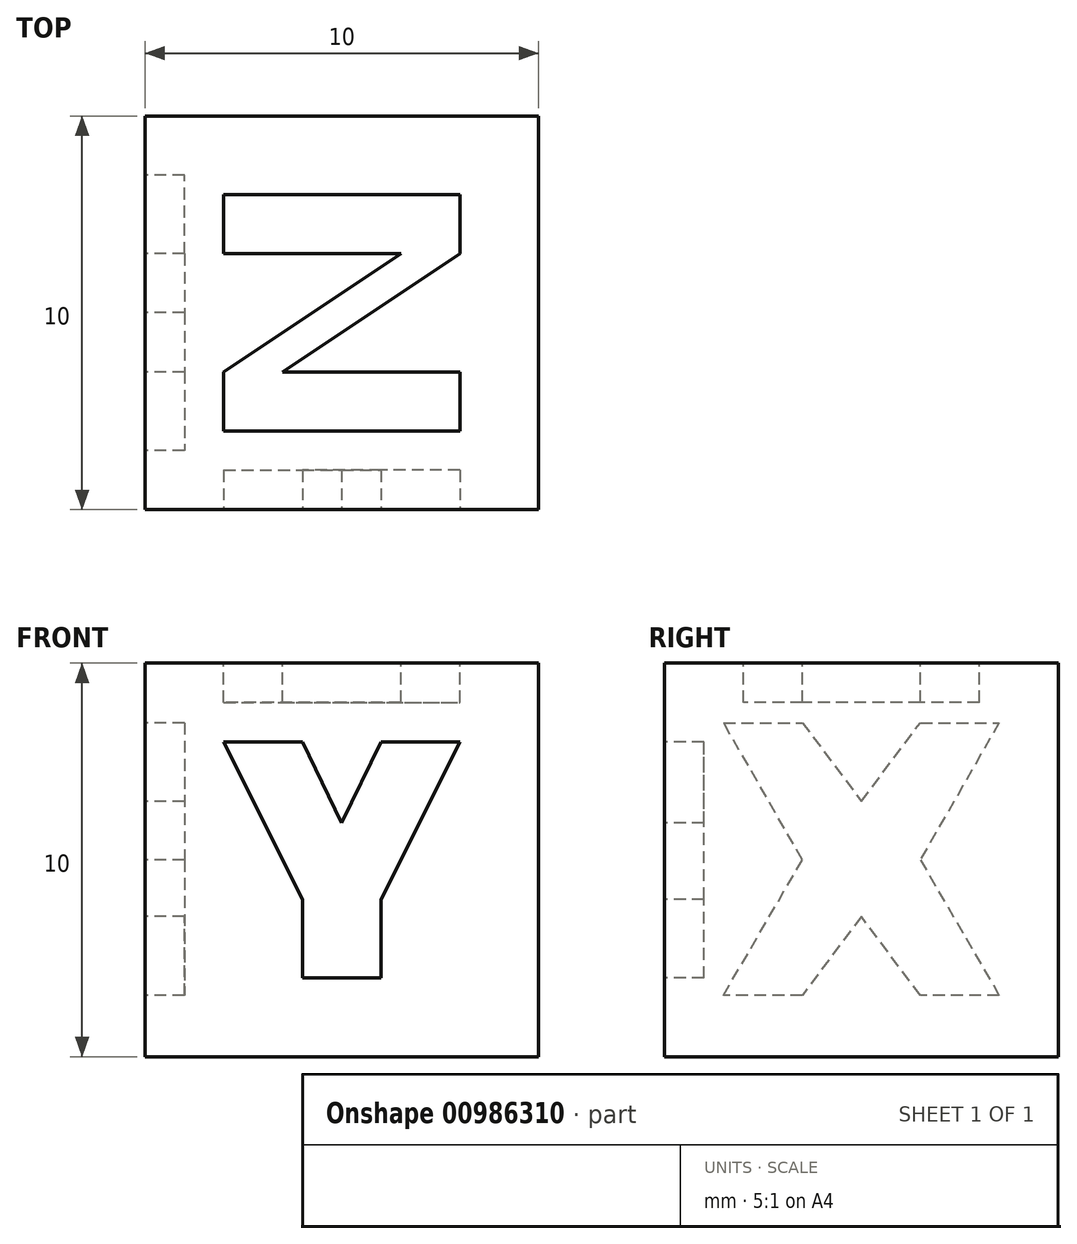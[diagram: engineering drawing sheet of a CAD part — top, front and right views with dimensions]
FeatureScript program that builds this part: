
annotation { "Feature Type Name" : "Feature", "Feature Type Description" : "" }
export const myFeature = defineFeature(function(context is Context, id is Id, definition is map)
    precondition{}
    {
        {
            var Q0;
            Q0=qCreatedBy(makeId("Top.planeOp"),FACE);
            var sketch = newSketch(context, id + "F0", { "sketchPlane" : qUnion([Q0])});
            skLineSegment(sketch, "E0.bottom", {"start": v(0, 0) * mm, "end": v(10, 0) * mm});
            skLineSegment(sketch, "E0.top", {"start": v(0, 10) * mm, "end": v(10, 10) * mm});
            skLineSegment(sketch, "E0.left", {"start": v(0, 0) * mm, "end": v(0, 10) * mm});
            skLineSegment(sketch, "E0.right", {"start": v(10, 0) * mm, "end": v(10, 10) * mm});
            skSolve(sketch);
        }
        {
            var Q0;
            Q0=makeQuery(id+"F0.imprint","IMPRINT",FACE,{"disambiguationData":[TD([[makeQuery(id+"F0.imprint","IMPRINT",EDGE,{"derivedFrom":sQuery(id+"F0.wireOp",EDGE,"E0.bottom")}),1.0]])]});
            extrude(context, id + "F1", {"entities" : qUnion([Q0]), "depth" : 10 * mm, "offsetDistance" : 25 * mm});
        }
        {
            var Q0;
            Q0=makeQuery(id+"F1.opExtrude","SWEPT_FACE",FACE,{"disambiguationData":[OSD([sQuery(id+"F0.wireOp",EDGE,"E0.bottom")])]});
            var sketch = newSketch(context, id + "F2", { "sketchPlane" : qUnion([Q0])});
            skLineSegment(sketch, "E1", {"start": v(2, 8) * mm, "end": v(4, 8) * mm});
            skLineSegment(sketch, "E2", {"start": v(4, 8) * mm, "end": v(5, 5.94) * mm});
            skLineSegment(sketch, "E3", {"start": v(5, 5.94) * mm, "end": v(6, 8) * mm});
            skLineSegment(sketch, "E4", {"start": v(6, 8) * mm, "end": v(8, 8) * mm});
            skLineSegment(sketch, "E5", {"start": v(8, 8) * mm, "end": v(6, 4) * mm});
            skLineSegment(sketch, "E6", {"start": v(6, 4) * mm, "end": v(6, 2) * mm});
            skLineSegment(sketch, "E7", {"start": v(6, 2) * mm, "end": v(4, 2) * mm});
            skLineSegment(sketch, "E8", {"start": v(4, 2) * mm, "end": v(4, 4) * mm});
            skLineSegment(sketch, "E9", {"start": v(4, 4) * mm, "end": v(2, 8) * mm});
            skLineSegment(sketch, "E10", {"start": v(5, 10) * mm, "end": v(5, 0) * mm, "construction": true});
            skSolve(sketch);
        }
        {
            var Q0;
            Q0=makeQuery(id+"F2.imprint","IMPRINT",FACE,{"disambiguationData":[TD([[makeQuery(id+"F2.imprint","IMPRINT",EDGE,{"derivedFrom":sQuery(id+"F2.wireOp",EDGE,"E1")}),-1.0]])]});
            extrude(context, id + "F3", {"entities" : qUnion([Q0]), "operationType" : NewBodyOperationType.REMOVE, "oppositeDirection" : true, "depth" : 1 * mm, "offsetDistance" : 25 * mm});
        }
        {
            var Q0;
            Q0=makeQuery(id+"F1.opExtrude","SWEPT_FACE",FACE,{"disambiguationData":[OSD([sQuery(id+"F0.wireOp",EDGE,"E0.left")])]});
            var sketch = newSketch(context, id + "F4", { "sketchPlane" : qUnion([Q0])});
            skLineSegment(sketch, "E11", {"start": v(-5, 10) * mm, "end": v(-5, 0) * mm, "construction": true});
            skLineSegment(sketch, "E12", {"start": v(-10, 5) * mm, "end": v(0, 5) * mm, "construction": true});
            skLineSegment(sketch, "E13", {"start": v(-8.5, 8.48) * mm, "end": v(-6.5, 5) * mm});
            skLineSegment(sketch, "E14", {"start": v(-6.5, 5) * mm, "end": v(-8.5, 1.56) * mm});
            skLineSegment(sketch, "E15", {"start": v(-8.5, 1.56) * mm, "end": v(-6.5, 1.56) * mm});
            skLineSegment(sketch, "E16", {"start": v(-6.5, 1.56) * mm, "end": v(-5, 3.56) * mm});
            skLineSegment(sketch, "E17", {"start": v(-5, 3.56) * mm, "end": v(-3.5, 1.56) * mm});
            skLineSegment(sketch, "E18", {"start": v(-3.5, 1.56) * mm, "end": v(-1.5, 1.56) * mm});
            skLineSegment(sketch, "E19", {"start": v(-1.5, 1.56) * mm, "end": v(-3.5, 5) * mm});
            skLineSegment(sketch, "E20", {"start": v(-3.5, 5) * mm, "end": v(-1.5, 8.48) * mm});
            skLineSegment(sketch, "E21", {"start": v(-1.5, 8.48) * mm, "end": v(-3.5, 8.48) * mm});
            skLineSegment(sketch, "E22", {"start": v(-3.5, 8.48) * mm, "end": v(-5, 6.48) * mm});
            skLineSegment(sketch, "E23", {"start": v(-5, 6.48) * mm, "end": v(-6.5, 8.48) * mm});
            skLineSegment(sketch, "E24", {"start": v(-6.5, 8.48) * mm, "end": v(-8.5, 8.48) * mm});
            skSolve(sketch);
        }
        {
            var Q0;
            Q0=makeQuery(id+"F4.imprint","IMPRINT",FACE,{"disambiguationData":[TD([[makeQuery(id+"F4.imprint","IMPRINT",EDGE,{"derivedFrom":sQuery(id+"F4.wireOp",EDGE,"E13")}),1.0]])]});
            extrude(context, id + "F5", {"entities" : qUnion([Q0]), "operationType" : NewBodyOperationType.REMOVE, "oppositeDirection" : true, "depth" : 1 * mm, "offsetDistance" : 25 * mm});
        }
        {
            var Q0;
            Q0=makeQuery(id+"F1.opExtrude","CAP_FACE",FACE,{"disambiguationData":[OSD([sQuery(id+"F0.wireOp",EDGE,"E0.bottom"),sQuery(id+"F0.wireOp",EDGE,"E0.top"),sQuery(id+"F0.wireOp",EDGE,"E0.left"),sQuery(id+"F0.wireOp",EDGE,"E0.right")])],"isStart":false});
            var sketch = newSketch(context, id + "F6", { "sketchPlane" : qUnion([Q0])});
            skLineSegment(sketch, "E25", {"start": v(5, 10) * mm, "end": v(5, 0) * mm, "construction": true});
            skLineSegment(sketch, "E26", {"start": v(0, 5) * mm, "end": v(10, 5) * mm, "construction": true});
            skLineSegment(sketch, "E27", {"start": v(2, 8) * mm, "end": v(8, 8) * mm});
            skLineSegment(sketch, "E28", {"start": v(3.5, 3.5) * mm, "end": v(8, 3.5) * mm});
            skLineSegment(sketch, "E29", {"start": v(8, 3.5) * mm, "end": v(8, 2) * mm});
            skLineSegment(sketch, "E30", {"start": v(8, 2) * mm, "end": v(2, 2) * mm});
            skLineSegment(sketch, "E31", {"start": v(2, 2) * mm, "end": v(2, 3.5) * mm});
            skLineSegment(sketch, "E32", {"start": v(2, 3.5) * mm, "end": v(6.5, 6.5) * mm});
            skLineSegment(sketch, "E33", {"start": v(6.5, 6.5) * mm, "end": v(2, 6.5) * mm});
            skLineSegment(sketch, "E34", {"start": v(2, 6.5) * mm, "end": v(2, 8) * mm});
            skLineSegment(sketch, "E35", {"start": v(8, 8) * mm, "end": v(8, 6.5) * mm});
            skLineSegment(sketch, "E36", {"start": v(8, 6.5) * mm, "end": v(3.5, 3.5) * mm});
            skSolve(sketch);
        }
        {
            var Q0;
            Q0=makeQuery(id+"F6.imprint","IMPRINT",FACE,{"disambiguationData":[TD([[makeQuery(id+"F6.imprint","IMPRINT",EDGE,{"derivedFrom":sQuery(id+"F6.wireOp",EDGE,"E27")}),-1.0]])]});
            extrude(context, id + "F7", {"entities" : qUnion([Q0]), "operationType" : NewBodyOperationType.REMOVE, "oppositeDirection" : true, "depth" : 1 * mm, "offsetDistance" : 25 * mm});
        }
    });
